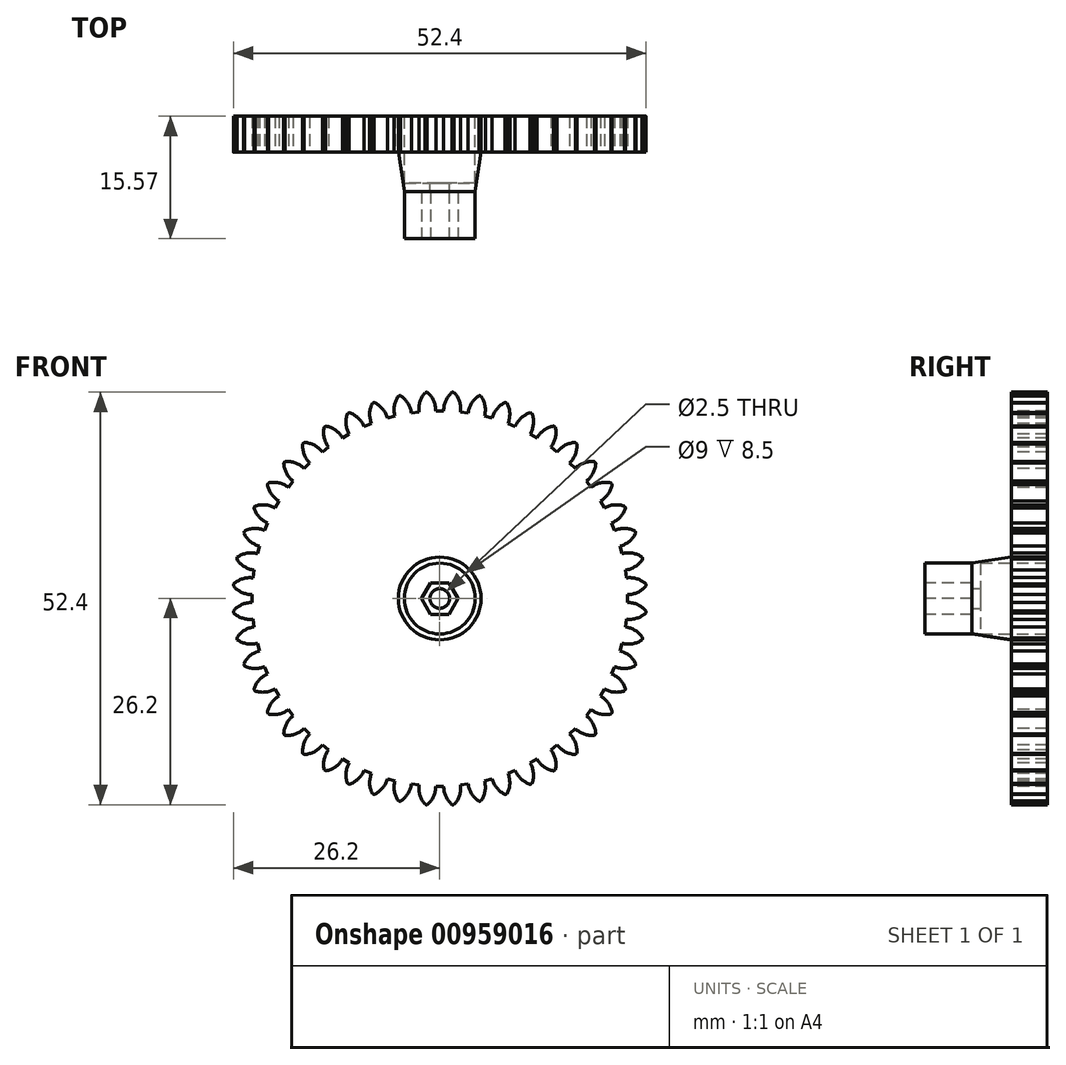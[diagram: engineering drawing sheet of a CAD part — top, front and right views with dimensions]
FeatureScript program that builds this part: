
annotation { "Feature Type Name" : "Feature", "Feature Type Description" : "" }
export const myFeature = defineFeature(function(context is Context, id is Id, definition is map)
    precondition{}
    {
        {
            var Q0;
            Q0=qCreatedBy(makeId("Front.planeOp"),FACE);
            var sketch = newSketch(context, id + "F0", { "sketchPlane" : qUnion([Q0])});
            skCircle(sketch, "E0", {"center": v(0, 0) * mm, "radius": 26.25 * mm});
            skSolve(sketch);
        }
        {
            var Q0;
            Q0=makeQuery(id+"F0.imprint","IMPRINT",FACE,{"disambiguationData":[TD([[makeQuery(id+"F0.imprint","IMPRINT",EDGE,{"derivedFrom":sQuery(id+"F0.wireOp",EDGE,"E0")}),1.0]])]});
            extrude(context, id + "F1", {"entities" : qUnion([Q0]), "depth" : 4.57 * mm, "offsetDistance" : 25.4 * mm});
        }
        {
            var Q0;
            Q0=makeQuery(id+"F1.opExtrude","CAP_FACE",FACE,{"disambiguationData":[OSD([sQuery(id+"F0.wireOp",EDGE,"E0")])],"isStart":false});
            var sketch = newSketch(context, id + "F2", { "sketchPlane" : qUnion([Q0])});
            skLineSegment(sketch, "E1", {"start": v(0, 26.25) * mm, "end": v(0, -26.25) * mm, "construction": true});
            skLineSegment(sketch, "E2", {"start": v(-10.97, 23.85) * mm, "end": v(10.97, 23.85) * mm});
            skArc(sketch, "E3", {"start": v(-0.5, 23.85) * mm, "mid": v(-0.78, 25.15) * mm, "end": v(-1.6, 26.2) * mm});
            skCircle(sketch, "E4", {"center": v(0, 0) * mm, "radius": 26.25 * mm});
            skArc(sketch, "E5.MirrorCS", {"start": v(0.5, 23.85) * mm, "mid": v(0.78, 25.15) * mm, "end": v(1.6, 26.2) * mm});
            skSolve(sketch);
        }
        {
            var Q0;
            {var subQ0=sQuery(id+"F2.wireOp",EDGE,"E3");Q0=makeQuery(id+"F2.imprint","IMPRINT",FACE,{"disambiguationData":[TD([[makeQuery(id+"F2.imprint","IMPRINT",EDGE,{"derivedFrom":subQ0}),-1.0]])]});}
            extrude(context, id + "F3", {"entities" : qUnion([Q0]), "operationType" : NewBodyOperationType.REMOVE, "endBound" : BoundingType.THROUGH_ALL, "oppositeDirection" : true, "depth" : 25.4 * mm, "offsetDistance" : 25.4 * mm});
        }
        {
            var Q0;
            Q0=makeQuery(id+"F3.boolean.opBoolean","COPY",FACE,{"derivedFrom":makeQuery(id+"F3.opExtrude","SWEPT_FACE",FACE,{"disambiguationData":[OSD([sQuery(id+"F2.wireOp",EDGE,"E3")])]})});
            var Q1;
            Q1=makeQuery(id+"F3.boolean.opBoolean","COPY",FACE,{"derivedFrom":makeQuery(id+"F3.opExtrude","SWEPT_FACE",FACE,{"disambiguationData":[OSD([sQuery(id+"F2.wireOp",EDGE,"E2")])]})});
            var Q2;
            Q2=makeQuery(id+"F3.boolean.opBoolean","COPY",FACE,{"derivedFrom":makeQuery(id+"F3.opExtrude","SWEPT_FACE",FACE,{"disambiguationData":[OSD([sQuery(id+"F2.wireOp",EDGE,"E5.MirrorCS")])]})});
            var Q3;
            Q3=makeQuery(id+"F1.opExtrude","SWEPT_FACE",FACE,{"disambiguationData":[OSD([sQuery(id+"F0.wireOp",EDGE,"E0")])]});
            circularPattern(context, id + "F4", {"patternType" : PatternType.FACE, "faces" : qUnion([Q0, Q1, Q2]), "axis" : qUnion([Q3]), "angle" : 360 * degree, "instanceCount" : 48, "equalSpace" : true});
        }
        {
            var Q0;
            Q0=makeQuery(id+"F1.opExtrude","CAP_FACE",FACE,{"disambiguationData":[OSD([sQuery(id+"F0.wireOp",EDGE,"E0")])],"isStart":false});
            var sketch = newSketch(context, id + "F5", { "sketchPlane" : qUnion([Q0])});
            skCircle(sketch, "E6.cCircle", {"center": v(0, 0) * mm, "radius": 2 * mm, "construction": true});
            skLineSegment(sketch, "E6.0", {"start": v(-1.15, 2) * mm, "end": v(1.15, 2) * mm, "construction": true});
            skLineSegment(sketch, "E6.1", {"start": v(1.15, 2) * mm, "end": v(2.3, 0) * mm, "construction": true});
            skLineSegment(sketch, "E6.2", {"start": v(2.3, 0) * mm, "end": v(1.15, -2) * mm, "construction": true});
            skLineSegment(sketch, "E6.3", {"start": v(1.15, -2) * mm, "end": v(-1.15, -2) * mm, "construction": true});
            skLineSegment(sketch, "E6.4", {"start": v(-1.15, -2) * mm, "end": v(-2.3, 0) * mm, "construction": true});
            skLineSegment(sketch, "E6.5", {"start": v(-2.3, 0) * mm, "end": v(-1.15, 2) * mm, "construction": true});
            skPoint(sketch, "E6.0.midPoint", {"position": v(0, 2) * mm});
            skCircle(sketch, "E7", {"center": v(0, 0) * mm, "radius": 5.25 * mm});
            skSolve(sketch);
        }
        {
            var Q0;
            Q0=makeQuery(id+"F5.imprint","IMPRINT",FACE,{"disambiguationData":[TD([[makeQuery(id+"F5.imprint","IMPRINT",EDGE,{"derivedFrom":sQuery(id+"F5.wireOp",EDGE,"E7")}),-1.0]])]});
            cPlane(context, id + "F6", {"entities" : qUnion([Q0]), "cplaneType" : CPlaneType.OFFSET, "offset" : 5 * mm, "width" : 152.4 * mm, "height" : 152.4 * mm});
        }
        {
            var Q0;
            Q0=qCreatedBy(id+"F6.planeOp",FACE);
            var sketch = newSketch(context, id + "F7", { "sketchPlane" : qUnion([Q0])});
            skCircle(sketch, "E8.cCircle", {"center": v(0, 0) * mm, "radius": 2 * mm, "construction": true});
            skLineSegment(sketch, "E8.0", {"start": v(-1.15, 2) * mm, "end": v(1.15, 2) * mm, "construction": true});
            skLineSegment(sketch, "E8.1", {"start": v(1.15, 2) * mm, "end": v(2.3, 0) * mm, "construction": true});
            skLineSegment(sketch, "E8.2", {"start": v(2.3, 0) * mm, "end": v(1.15, -2) * mm, "construction": true});
            skLineSegment(sketch, "E8.3", {"start": v(1.15, -2) * mm, "end": v(-1.15, -2) * mm, "construction": true});
            skLineSegment(sketch, "E8.4", {"start": v(-1.15, -2) * mm, "end": v(-2.3, 0) * mm, "construction": true});
            skLineSegment(sketch, "E8.5", {"start": v(-2.3, 0) * mm, "end": v(-1.15, 2) * mm, "construction": true});
            skPoint(sketch, "E8.0.midPoint", {"position": v(0, 2) * mm});
            skCircle(sketch, "E9", {"center": v(0, 0) * mm, "radius": 4.5 * mm});
            skSolve(sketch);
        }
        {
            var Q1;
            Q1=makeQuery(id+"F5.imprint","IMPRINT",FACE,{"disambiguationData":[TD([[makeQuery(id+"F5.imprint","IMPRINT",EDGE,{"derivedFrom":sQuery(id+"F5.wireOp",EDGE,"E7")}),1.0]])]});
            var Q2;
            Q2=makeQuery(id+"F7.imprint","IMPRINT",FACE,{"disambiguationData":[TD([[makeQuery(id+"F7.imprint","IMPRINT",EDGE,{"derivedFrom":sQuery(id+"F7.wireOp",EDGE,"E9")}),1.0]])]});
            loft(context, id + "F8", {"operationType" : NewBodyOperationType.ADD, "sheetProfilesArray" : [{ "sheetProfileEntities" : qUnion([Q1]) }, { "sheetProfileEntities" : qUnion([Q2]) }]});
        }
        {
            var Q0;
            Q0=makeQuery(id+"F8.opLoft","CAP_FACE",FACE,{"disambiguationData":[OSD([makeQuery(id+"F7.imprint","IMPRINT",FACE,{"disambiguationData":[TD([[makeQuery(id+"F7.imprint","IMPRINT",EDGE,{"derivedFrom":sQuery(id+"F7.wireOp",EDGE,"E9")}),1.0]])]})])],"isStart":true});
            extrude(context, id + "F9", {"entities" : qUnion([Q0]), "operationType" : NewBodyOperationType.ADD, "depth" : 6 * mm, "offsetDistance" : 25.4 * mm});
        }
        {
            var Q0;
            Q0=makeQuery(id+"F1.opExtrude","CAP_FACE",FACE,{"disambiguationData":[OSD([sQuery(id+"F0.wireOp",EDGE,"E0")])],"isStart":true});
            var sketch = newSketch(context, id + "F10", { "sketchPlane" : qUnion([Q0])});
            skCircle(sketch, "E10.cCircle", {"center": v(0, 0) * mm, "radius": 2 * mm, "construction": true});
            skLineSegment(sketch, "E10.0", {"start": v(-1.15, 2) * mm, "end": v(1.15, 2) * mm, "construction": true});
            skLineSegment(sketch, "E10.1", {"start": v(1.15, 2) * mm, "end": v(2.3, 0) * mm, "construction": true});
            skLineSegment(sketch, "E10.2", {"start": v(2.3, 0) * mm, "end": v(1.15, -2) * mm, "construction": true});
            skLineSegment(sketch, "E10.3", {"start": v(1.15, -2) * mm, "end": v(-1.15, -2) * mm, "construction": true});
            skLineSegment(sketch, "E10.4", {"start": v(-1.15, -2) * mm, "end": v(-2.3, 0) * mm, "construction": true});
            skLineSegment(sketch, "E10.5", {"start": v(-2.3, 0) * mm, "end": v(-1.15, 2) * mm, "construction": true});
            skPoint(sketch, "E10.0.midPoint", {"position": v(0, 2) * mm});
            skCircle(sketch, "E11", {"center": v(0, 0) * mm, "radius": 4.5 * mm});
            skSolve(sketch);
        }
        {
            var Q0;
            Q0=makeQuery(id+"F10.imprint","IMPRINT",FACE,{"disambiguationData":[TD([[makeQuery(id+"F10.imprint","IMPRINT",EDGE,{"derivedFrom":sQuery(id+"F10.wireOp",EDGE,"E11")}),1.0]])]});
            extrude(context, id + "F11", {"entities" : qUnion([Q0]), "operationType" : NewBodyOperationType.REMOVE, "oppositeDirection" : true, "depth" : 8.5 * mm, "offsetDistance" : 25.4 * mm});
        }
        {
            var Q0;
            Q0=makeQuery(id+"F11.boolean.opBoolean","COPY",FACE,{"derivedFrom":makeQuery(id+"F11.opExtrude","CAP_FACE",FACE,{"disambiguationData":[OSD([sQuery(id+"F10.wireOp",EDGE,"E11")])],"isStart":false})});
            var sketch = newSketch(context, id + "F12", { "sketchPlane" : qUnion([Q0])});
            skCircle(sketch, "E12", {"center": v(0, 0) * mm, "radius": 1.25 * mm});
            skSolve(sketch);
        }
        {
            var Q0;
            Q0=makeQuery(id+"F12.imprint","IMPRINT",FACE,{"disambiguationData":[TD([[makeQuery(id+"F12.imprint","IMPRINT",EDGE,{"derivedFrom":sQuery(id+"F12.wireOp",EDGE,"E12")}),1.0]])]});
            extrude(context, id + "F13", {"entities" : qUnion([Q0]), "operationType" : NewBodyOperationType.REMOVE, "endBound" : BoundingType.THROUGH_ALL, "oppositeDirection" : true, "depth" : 25.4 * mm, "offsetDistance" : 25.4 * mm});
        }
        {
            var Q0;
            Q0=makeQuery(id+"F9.opExtrude","CAP_FACE",FACE,{"disambiguationData":[OSD([makeQuery(id+"F7.imprint","IMPRINT",FACE,{"disambiguationData":[TD([[makeQuery(id+"F7.imprint","IMPRINT",EDGE,{"derivedFrom":sQuery(id+"F7.wireOp",EDGE,"E9")}),1.0]])]})])],"isStart":false});
            var sketch = newSketch(context, id + "F14", { "sketchPlane" : qUnion([Q0])});
            skCircle(sketch, "E13.cCircle", {"center": v(0, 0) * mm, "radius": 2 * mm, "construction": true});
            skLineSegment(sketch, "E13.0", {"start": v(-1.15, 2) * mm, "end": v(1.15, 2) * mm});
            skLineSegment(sketch, "E13.1", {"start": v(1.15, 2) * mm, "end": v(2.3, 0) * mm});
            skLineSegment(sketch, "E13.2", {"start": v(2.3, 0) * mm, "end": v(1.15, -2) * mm});
            skLineSegment(sketch, "E13.3", {"start": v(1.15, -2) * mm, "end": v(-1.15, -2) * mm});
            skLineSegment(sketch, "E13.4", {"start": v(-1.15, -2) * mm, "end": v(-2.3, 0) * mm});
            skLineSegment(sketch, "E13.5", {"start": v(-2.3, 0) * mm, "end": v(-1.15, 2) * mm});
            skPoint(sketch, "E13.0.midPoint", {"position": v(0, 2) * mm});
            skSolve(sketch);
        }
        {
            var Q0;
            Q0=makeQuery(id+"F14.imprint","IMPRINT",FACE,{"disambiguationData":[TD([[makeQuery(id+"F14.imprint","IMPRINT",EDGE,{"derivedFrom":sQuery(id+"F14.wireOp",EDGE,"E13.0")}),-1.0]])]});
            extrude(context, id + "F15", {"entities" : qUnion([Q0]), "operationType" : NewBodyOperationType.REMOVE, "oppositeDirection" : true, "depth" : 6 * mm, "offsetDistance" : 25.4 * mm});
        }
    });
